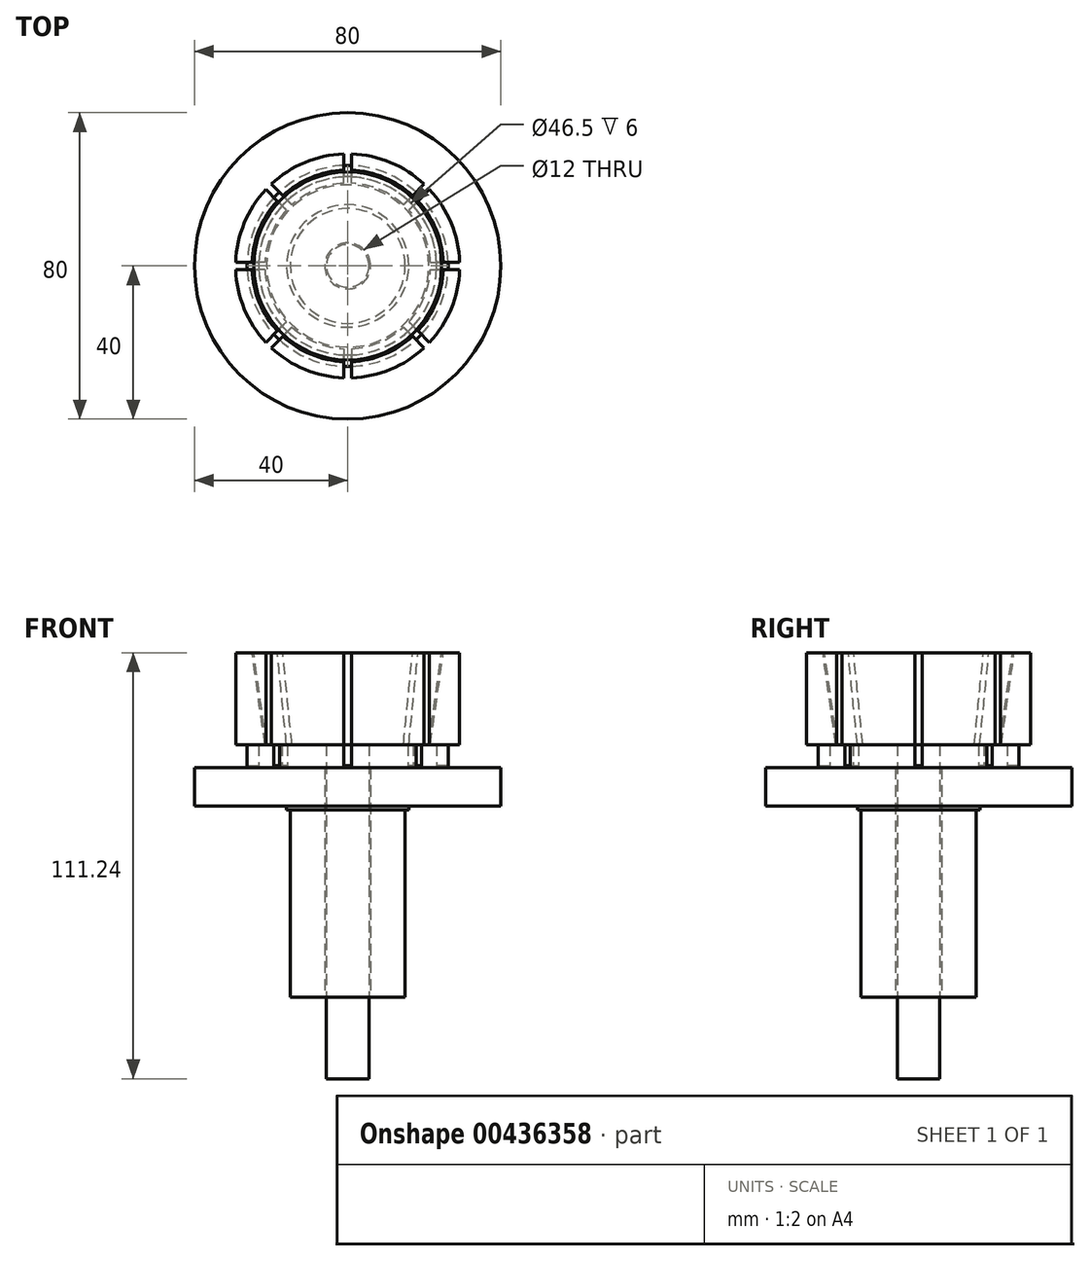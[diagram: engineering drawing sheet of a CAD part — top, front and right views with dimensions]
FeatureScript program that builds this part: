
annotation { "Feature Type Name" : "Feature", "Feature Type Description" : "" }
export const myFeature = defineFeature(function(context is Context, id is Id, definition is map)
    precondition{}
    {
        {
            var Q0;
            Q0=qCreatedBy(makeId("Right.planeOp"),FACE);
            var sketch = newSketch(context, id + "F0", { "sketchPlane" : qUnion([Q0])});
            skLineSegment(sketch, "E0", {"start": v(6, -50) * mm, "end": v(15, -50) * mm});
            skLineSegment(sketch, "E1", {"start": v(15, -50) * mm, "end": v(15, -1) * mm});
            skLineSegment(sketch, "E2", {"start": v(15, -1) * mm, "end": v(16, -1) * mm});
            skLineSegment(sketch, "E3", {"start": v(16, -1) * mm, "end": v(16, 0) * mm});
            skLineSegment(sketch, "E4", {"start": v(16, 0) * mm, "end": v(40, 0) * mm});
            skLineSegment(sketch, "E5", {"start": v(40, 0) * mm, "end": v(40, 10) * mm});
            skLineSegment(sketch, "E6", {"start": v(40, 10) * mm, "end": v(26.25, 10) * mm});
            skLineSegment(sketch, "E7", {"start": v(26.25, 10) * mm, "end": v(26.25, 16) * mm});
            skLineSegment(sketch, "E8", {"start": v(26.25, 16) * mm, "end": v(29.25, 16) * mm});
            skLineSegment(sketch, "E9", {"start": v(29.25, 16) * mm, "end": v(29.25, 40) * mm});
            skLineSegment(sketch, "E10", {"start": v(29.25, 40) * mm, "end": v(25, 40) * mm});
            skLineSegment(sketch, "E11", {"start": v(25, 40) * mm, "end": v(21.63, 16) * mm});
            skLineSegment(sketch, "E12", {"start": v(23.25, 16) * mm, "end": v(23.25, 10) * mm});
            skLineSegment(sketch, "E13", {"start": v(23.25, 10) * mm, "end": v(6, 10) * mm});
            skLineSegment(sketch, "E14", {"start": v(6, 10) * mm, "end": v(6, -50) * mm});
            skLineSegment(sketch, "E15", {"start": v(0, -50) * mm, "end": v(0, 40) * mm, "construction": true});
            skLineSegment(sketch, "E16", {"start": v(23.25, 16) * mm, "end": v(21.63, 16) * mm});
            skSolve(sketch);
        }
        {
            var Q0;
            Q0 = qSketchRegion(id + "F0", true);
            var Q1;
            Q1=sQuery(id+"F0.wireOp",EDGE,"E15");
            revolve(context, id + "F1", {"entities" : qUnion([Q0]), "axis" : qUnion([Q1]), "revolveType" : RevolveType.FULL});
        }
        {
            var Q0;
            Q0=makeQuery(id+"F1.opRevolve","SWEPT_FACE",FACE,{"disambiguationData":[OSD([sQuery(id+"F0.wireOp",EDGE,"E6")])]});
            cPlane(context, id + "F2", {"entities" : qUnion([Q0]), "cplaneType" : CPlaneType.OFFSET, "offset" : .5 * mm, "width" : 150 * mm, "height" : 150 * mm});
        }
        {
            var Q0;
            Q0=qCreatedBy(id+"F2.planeOp",FACE);
            var sketch = newSketch(context, id + "F3", { "sketchPlane" : qUnion([Q0])});
            skLineSegment(sketch, "E17.bottom", {"start": v(-40, 1) * mm, "end": v(-5.92, 1) * mm});
            skLineSegment(sketch, "E17.top", {"start": v(-40, -1) * mm, "end": v(-5.92, -1) * mm});
            skLineSegment(sketch, "E17.left", {"start": v(-40, 1) * mm, "end": v(-40, -1) * mm});
            skLineSegment(sketch, "E17.right", {"start": v(-5.92, 1) * mm, "end": v(-5.92, -1) * mm});
            skPoint(sketch, "E17.middle", {"position": v(-22.96, 0) * mm});
            skLineSegment(sketch, "E18.1.0", {"start": v(-29, -27.58) * mm, "end": v(-4.9, -3.48) * mm});
            skLineSegment(sketch, "E18.1.1", {"start": v(-4.9, -3.48) * mm, "end": v(-3.48, -4.9) * mm});
            skLineSegment(sketch, "E18.1.2", {"start": v(-27.58, -29) * mm, "end": v(-3.48, -4.9) * mm});
            skLineSegment(sketch, "E18.1.3", {"start": v(-29, -27.58) * mm, "end": v(-27.58, -29) * mm});
            skLineSegment(sketch, "E18.2.0", {"start": v(-1, -40) * mm, "end": v(-1, -5.92) * mm});
            skLineSegment(sketch, "E18.2.1", {"start": v(-1, -5.92) * mm, "end": v(1, -5.92) * mm});
            skLineSegment(sketch, "E18.2.2", {"start": v(1, -40) * mm, "end": v(1, -5.92) * mm});
            skLineSegment(sketch, "E18.2.3", {"start": v(-1, -40) * mm, "end": v(1, -40) * mm});
            skLineSegment(sketch, "E18.3.0", {"start": v(27.58, -29) * mm, "end": v(3.48, -4.9) * mm});
            skLineSegment(sketch, "E18.3.1", {"start": v(3.48, -4.9) * mm, "end": v(4.9, -3.48) * mm});
            skLineSegment(sketch, "E18.3.2", {"start": v(29, -27.58) * mm, "end": v(4.9, -3.48) * mm});
            skLineSegment(sketch, "E18.3.3", {"start": v(27.58, -29) * mm, "end": v(29, -27.58) * mm});
            skLineSegment(sketch, "E18.4.0", {"start": v(40, -1) * mm, "end": v(5.92, -1) * mm});
            skLineSegment(sketch, "E18.4.1", {"start": v(5.92, -1) * mm, "end": v(5.92, 1) * mm});
            skLineSegment(sketch, "E18.4.2", {"start": v(40, 1) * mm, "end": v(5.92, 1) * mm});
            skLineSegment(sketch, "E18.4.3", {"start": v(40, -1) * mm, "end": v(40, 1) * mm});
            skLineSegment(sketch, "E18.5.0", {"start": v(29, 27.58) * mm, "end": v(4.9, 3.48) * mm});
            skLineSegment(sketch, "E18.5.1", {"start": v(4.9, 3.48) * mm, "end": v(3.48, 4.9) * mm});
            skLineSegment(sketch, "E18.5.2", {"start": v(27.58, 29) * mm, "end": v(3.48, 4.9) * mm});
            skLineSegment(sketch, "E18.5.3", {"start": v(29, 27.58) * mm, "end": v(27.58, 29) * mm});
            skLineSegment(sketch, "E18.6.0", {"start": v(1, 40) * mm, "end": v(1, 5.92) * mm});
            skLineSegment(sketch, "E18.6.1", {"start": v(1, 5.92) * mm, "end": v(-1, 5.92) * mm});
            skLineSegment(sketch, "E18.6.2", {"start": v(-1, 40) * mm, "end": v(-1, 5.92) * mm});
            skLineSegment(sketch, "E18.6.3", {"start": v(1, 40) * mm, "end": v(-1, 40) * mm});
            skLineSegment(sketch, "E18.7.0", {"start": v(-27.58, 29) * mm, "end": v(-3.48, 4.9) * mm});
            skLineSegment(sketch, "E18.7.1", {"start": v(-3.48, 4.9) * mm, "end": v(-4.9, 3.48) * mm});
            skLineSegment(sketch, "E18.7.2", {"start": v(-29, 27.58) * mm, "end": v(-4.9, 3.48) * mm});
            skLineSegment(sketch, "E18.7.3", {"start": v(-27.58, 29) * mm, "end": v(-29, 27.58) * mm});
            skPoint(sketch, "E18.center", {"position": v(0, 0) * mm});
            skSolve(sketch);
        }
        {
            var Q0;
            Q0 = qSketchRegion(id + "F3", true);
            var Q1;
            Q1=makeQuery(id+"F1.opRevolve","SWEPT_FACE",FACE,{"disambiguationData":[OSD([sQuery(id+"F0.wireOp",EDGE,"E10")])]});
            extrude(context, id + "F4", {"entities" : qUnion([Q0]), "operationType" : NewBodyOperationType.REMOVE, "endBound" : BoundingType.UP_TO_SURFACE, "endBoundEntityFace" : qUnion([Q1]), "depth" : 25 * mm});
        }
        {
            var Q0;
            Q0=qCreatedBy(makeId("Right.planeOp"),FACE);
            var sketch = newSketch(context, id + "F5", { "sketchPlane" : qUnion([Q0])});
            skLineSegment(sketch, "E19", {"start": v(0, 40) * mm, "end": v(24.56, 40) * mm});
            skLineSegment(sketch, "E20", {"start": v(24.56, 40) * mm, "end": v(21.19, 16) * mm});
            skLineSegment(sketch, "E21", {"start": v(21.19, 16) * mm, "end": v(5.57, 16) * mm});
            skLineSegment(sketch, "E22", {"start": v(5.57, 16) * mm, "end": v(5.57, -71.24) * mm});
            skLineSegment(sketch, "E23", {"start": v(5.57, -71.24) * mm, "end": v(0, -71.24) * mm});
            skLineSegment(sketch, "E24", {"start": v(0, -71.24) * mm, "end": v(0, 40) * mm});
            skSolve(sketch);
        }
        {
            var Q0;
            Q0 = qSketchRegion(id + "F5", true);
            var Q1;
            Q1=sQuery(id+"F5.wireOp",EDGE,"E24");
            revolve(context, id + "F6", {"entities" : qUnion([Q0]), "axis" : qUnion([Q1]), "revolveType" : RevolveType.FULL});
        }
    });
